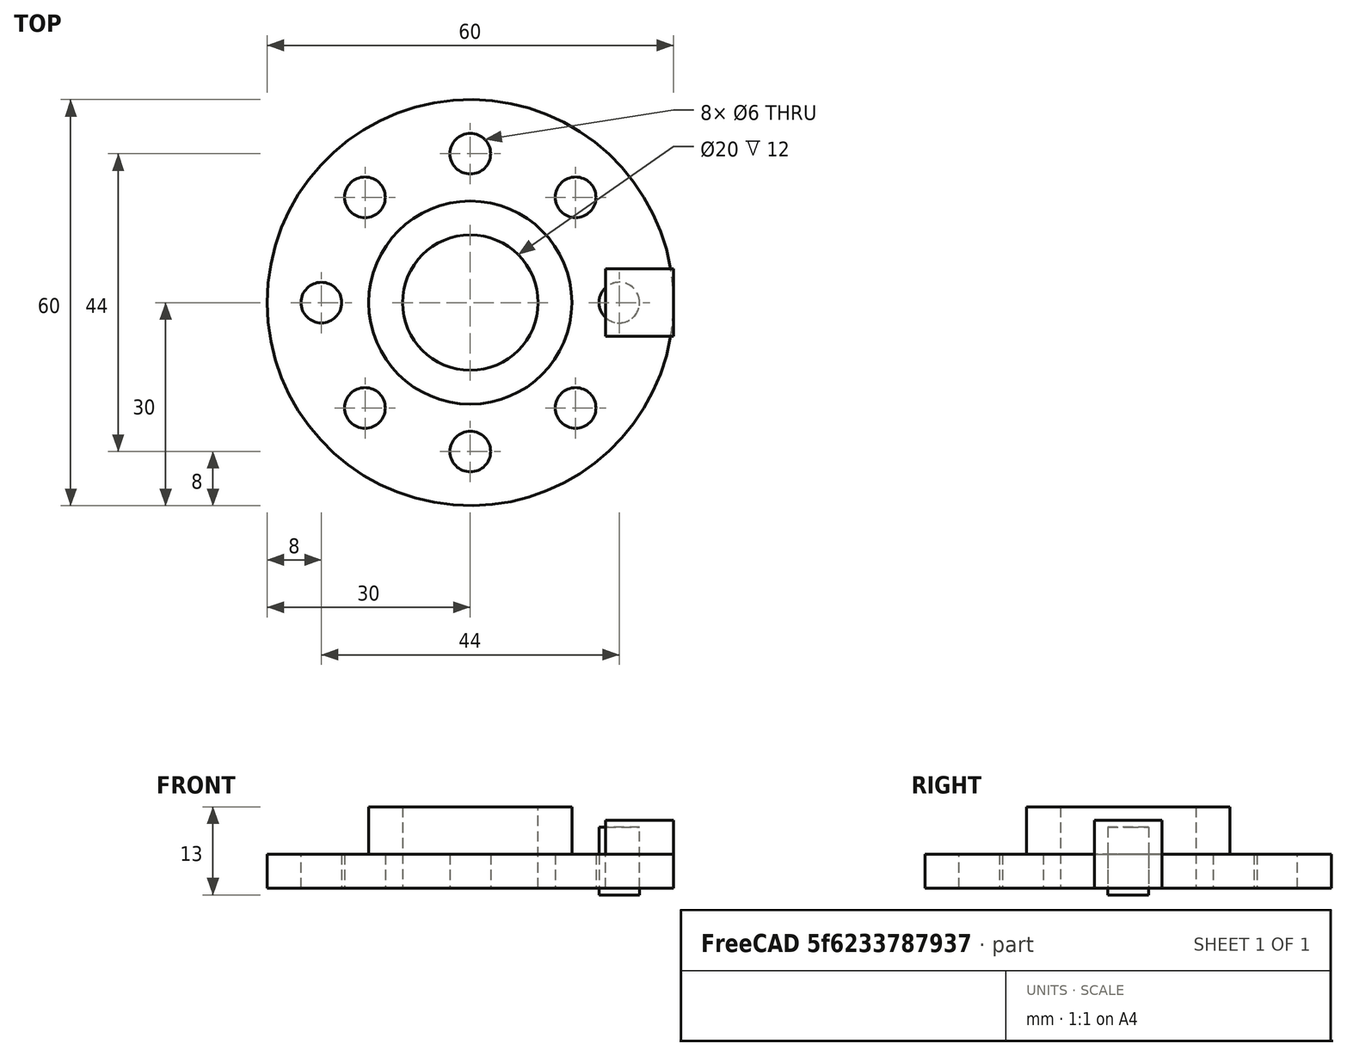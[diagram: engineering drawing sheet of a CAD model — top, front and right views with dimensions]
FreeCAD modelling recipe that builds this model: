
FCSTD DOCUMENT  (FreeCAD 0.21R33694 (Git))
Label: OJT1_T011R01
License: All rights reserved
LicenseURL: https://en.wikipedia.org/wiki/All_rights_reserved
objects: Part::Cylinder×4, Part::FeaturePython×2, Part::Cut×2, Part::Box×1, Part::MultiFuse×1, Part::Refine×1
note: 9 computed .brp shape members not serialized (recipe doc carries the construction recipe); baked Part::Feature solids carry a one-line shape summary decoded from their .brp

FEATURE [Part::Box] Box  label="Cub"
  AttacherType = Attacher::AttachEngine3D
  Height = 10
  Length = 10
  Placement = pos=(20,-5,0) rot=(0,0,1;0rad)
  Width = 10
  expr: .Placement.Base.x = 20
  expr: .Placement.Base.y = -5
FEATURE [Part::FeaturePython] Array  # Draft array (typed FeaturePython)
  AlwaysSyncPlacement = false
  Angle = 180
  ArrayType = 1
  Axis = (0,0,1)
  Base = -> Box
  Center = (0,0,0)
  Count = 6
  ExpandArray = false
  Fuse = false
  IntervalAxis = (0,0,0)
  IntervalX = (100,0,0)
  IntervalY = (0,100,0)
  IntervalZ = (0,0,100)
  NumberCircles = 3
  NumberPolar = 6
  NumberX = 2
  NumberY = 2
  NumberZ = 1
  PlacementList = 6 placements: [(20,-5,0),(19.1193,7.71062,0),(10.9356,17.476,0),(-1.42506,20.5662,0),(-13.2414,15.8008,0),(-20,5,0)]
  RadialDistance = 50
  ScaleList = (6) [(1,1,1),(1,1,1),(1,1,1),(1,1,1),(1,1,1),(1,1,1)]
  Symmetry = 1
  TangentialDistance = 25
FEATURE [Part::Cylinder] Cylinder  label="Base"
  Angle = 360
  AttacherType = Attacher::AttachEngine3D
  FirstAngle = 0
  Height = 12
  Radius = 15
  SecondAngle = 0
FEATURE [Part::Cylinder] Cylinder001  label="Tubo"
  Angle = 360
  AttacherType = Attacher::AttachEngine3D
  FirstAngle = 0
  Height = 5
  Radius = 30
  SecondAngle = 0
FEATURE [Part::MultiFuse] Fusion
  Shapes = -> [Cylinder,Cylinder001]
FEATURE [Part::Cylinder] Cylinder002  label="Tubo interior"
  Angle = 360
  AttacherType = Attacher::AttachEngine3D
  FirstAngle = 0
  Height = 30
  Placement = pos=(0,0,-1) rot=(0,0,1;0rad)
  Radius = 10
  SecondAngle = 0
FEATURE [Part::Cut] Cut
  Base = -> Fusion
  Tool = -> Cylinder002
FEATURE [Part::Refine] Cut001
  Source = -> Cut
FEATURE [Part::Cylinder] Cylinder003  label="Taladro_master"
  Angle = 360
  AttacherType = Attacher::AttachEngine3D
  FirstAngle = 0
  Height = 10
  Placement = pos=(22,0,-1) rot=(0,0,1;0rad)
  Radius = 3
  SecondAngle = 0
  expr: .Placement.Base.x = 22
FEATURE [Part::FeaturePython] Array001  # Draft array (typed FeaturePython)
  AlwaysSyncPlacement = false
  Angle = 360
  ArrayType = 1
  Axis = (0,0,1)
  Base = -> Cylinder003
  Center = (0,0,0)
  Count = 8
  ExpandArray = false
  Fuse = false
  IntervalAxis = (0,0,0)
  IntervalX = (100,0,0)
  IntervalY = (0,100,0)
  IntervalZ = (0,0,100)
  NumberCircles = 3
  NumberPolar = 8
  NumberX = 2
  NumberY = 2
  NumberZ = 1
  PlacementList = 8 placements: [(22,0,-1),(15.5563,15.5563,-1),(0,22,-1),(-15.5563,15.5563,-1),(-22,2.69422e-15,-1),(-15.5563,-15.5563,-1),(-4.88498e-15,-22,-1),(15.5563,-15.5563,-1)]
  RadialDistance = 50
  ScaleList = (8) [(1,1,1),(1,1,1),(1,1,1),(1,1,1),(1,1,1),(1,1,1),(1,1,1),(1,1,1)]
  Symmetry = 1
  TangentialDistance = 25
FEATURE [Part::Cut] Cut002
  Base = -> Cut001
  Tool = -> Array001
